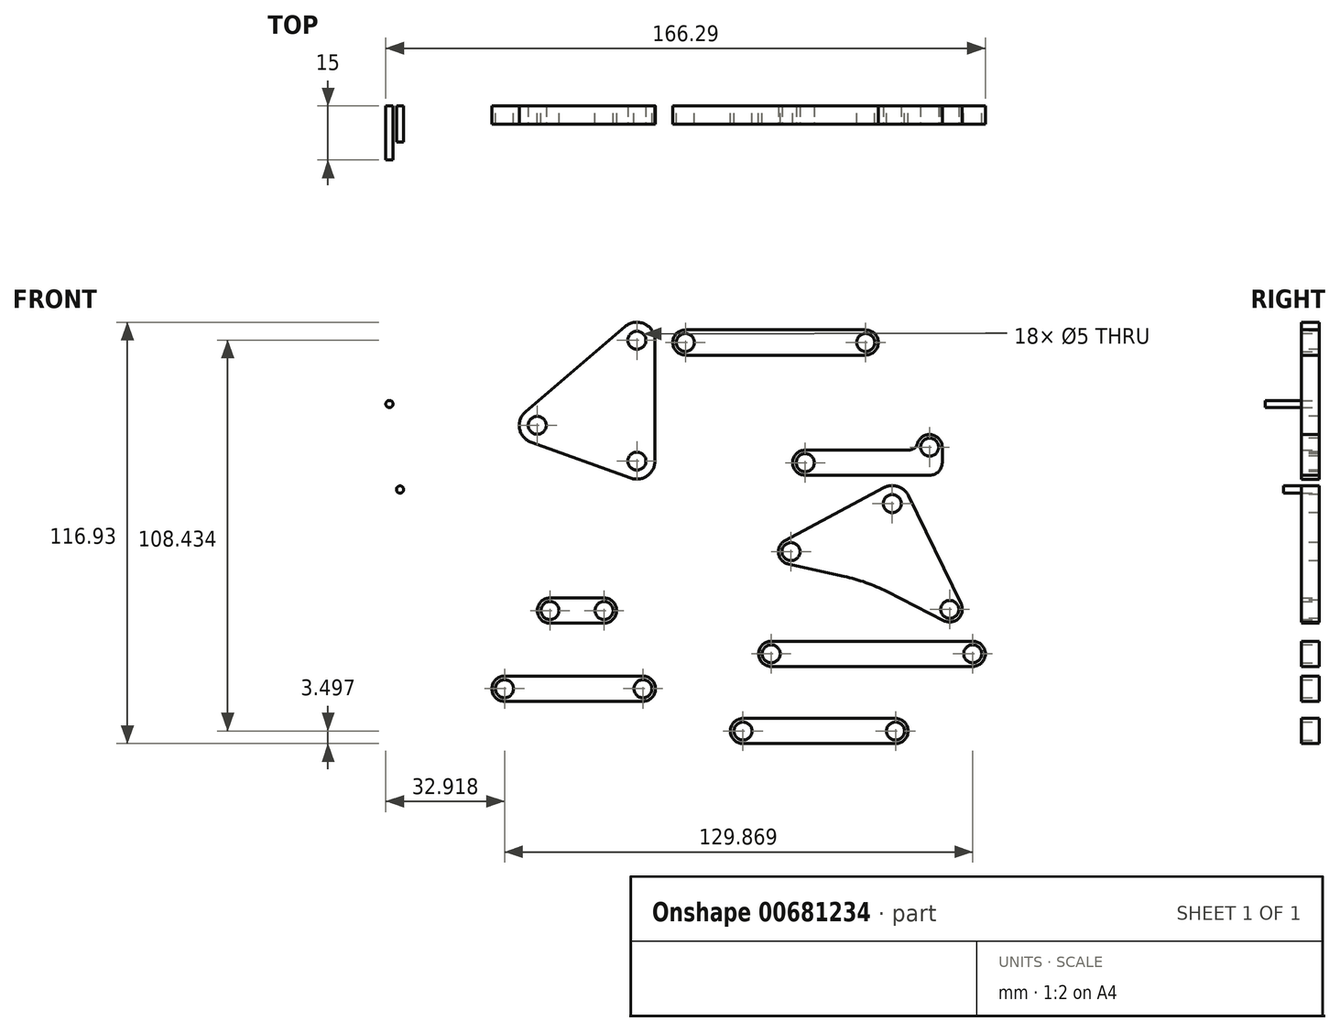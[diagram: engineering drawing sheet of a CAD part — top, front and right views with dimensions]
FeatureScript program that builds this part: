
annotation { "Feature Type Name" : "Feature", "Feature Type Description" : "" }
export const myFeature = defineFeature(function(context is Context, id is Id, definition is map)
    precondition{}
    {
        {
            var Q0;
            Q0=qCreatedBy(makeId("Front.planeOp"),FACE);
            var sketch = newSketch(context, id + "F0", { "sketchPlane" : qUnion([Q0])});
            skLineSegment(sketch, "E0", {"start": v(-19.3, 64.97) * mm, "end": v(-19.3, 13.47) * mm});
            skLineSegment(sketch, "E1", {"start": v(-19.3, 13.47) * mm, "end": v(-61.74, 28.74) * mm});
            skLineSegment(sketch, "E2", {"start": v(-61.74, 28.74) * mm, "end": v(-19.3, 64.97) * mm});
            skSolve(sketch);
        }
        {
            var Q0;
            Q0=makeQuery(id+"F0.imprint","IMPRINT",FACE,{"disambiguationData":[TD([[makeQuery(id+"F0.imprint","IMPRINT",EDGE,{"derivedFrom":sQuery(id+"F0.wireOp",EDGE,"E0")}),-1.0]])]});
            extrude(context, id + "F1", {"entities" : qUnion([Q0]), "depth" : 5 * mm, "offsetDistance" : 25 * mm});
        }
        {
            var Q0;
            Q0=makeQuery(id+"F1.opExtrude","SWEPT_EDGE",EDGE,{"disambiguationData":[OSD([sQuery(id+"F0.wireOp",EDGE,"E0"),sQuery(id+"F0.wireOp",EDGE,"E2")])]});
            var Q1;
            Q1=makeQuery(id+"F1.opExtrude","SWEPT_EDGE",EDGE,{"disambiguationData":[OSD([sQuery(id+"F0.wireOp",EDGE,"E0"),sQuery(id+"F0.wireOp",EDGE,"E1")])]});
            var Q2;
            Q2=makeQuery(id+"F1.opExtrude","SWEPT_EDGE",EDGE,{"disambiguationData":[OSD([sQuery(id+"F0.wireOp",EDGE,"E1"),sQuery(id+"F0.wireOp",EDGE,"E2")])]});
            fillet(context, id + "F2", {"entities" : qUnion([Q0, Q1, Q2]), "radius" : 5 * mm, "tangentPropagation" : true, "allowEdgeOverflow" : false});
        }
        {
            var Q0;
            Q0=makeQuery(id+"F1.opExtrude","CAP_FACE",FACE,{"disambiguationData":[OSD([sQuery(id+"F0.wireOp",EDGE,"E0"),sQuery(id+"F0.wireOp",EDGE,"E1"),sQuery(id+"F0.wireOp",EDGE,"E2")])],"isStart":false});
            var sketch = newSketch(context, id + "F3", { "sketchPlane" : qUnion([Q0])});
            skCircle(sketch, "E3", {"center": v(-24.3, 54.13) * mm, "radius": 2.5 * mm});
            skCircle(sketch, "E4", {"center": v(-24.3, 20.59) * mm, "radius": 2.5 * mm});
            skCircle(sketch, "E5", {"center": v(-51.95, 30.53) * mm, "radius": 2.5 * mm});
            skSolve(sketch);
        }
        {
            var Q0;
            Q0 = qSketchRegion(id + "F3", true);
            extrude(context, id + "F4", {"entities" : qUnion([Q0]), "operationType" : NewBodyOperationType.REMOVE, "oppositeDirection" : true, "depth" : 25 * mm, "offsetDistance" : 25 * mm});
        }
        {
            var Q0;
            Q0=qCreatedBy(makeId("Front.planeOp"),FACE);
            var sketch = newSketch(context, id + "F5", { "sketchPlane" : qUnion([Q0])});
            skLineSegment(sketch, "E6", {"start": v(22.4, 16.66) * mm, "end": v(60.4, 16.66) * mm});
            skLineSegment(sketch, "E7", {"start": v(60.4, 16.66) * mm, "end": v(60.4, 24.46) * mm});
            skLineSegment(sketch, "E8.0", {"start": v(22.4, 23.66) * mm, "end": v(53.4, 23.66) * mm});
            skLineSegment(sketch, "E9.0", {"start": v(53.4, 23.66) * mm, "end": v(53.4, 24.46) * mm});
            skArc(sketch, "E10", {"start": v(60.4, 24.46) * mm, "mid": v(56.9, 27.96) * mm, "end": v(53.4, 24.46) * mm});
            skArc(sketch, "E11", {"start": v(22.4, 23.66) * mm, "mid": v(18.9, 20.16) * mm, "end": v(22.4, 16.66) * mm});
            skSolve(sketch);
        }
        {
            var Q0;
            Q0=makeQuery(id+"F5.imprint","IMPRINT",FACE,{"disambiguationData":[TD([[makeQuery(id+"F5.imprint","IMPRINT",EDGE,{"derivedFrom":sQuery(id+"F5.wireOp",EDGE,"E6")}),1.0]])]});
            extrude(context, id + "F6", {"entities" : qUnion([Q0]), "depth" : 5 * mm, "offsetDistance" : 25 * mm});
        }
        {
            var Q0;
            Q0=makeQuery(id+"F6.opExtrude","SWEPT_EDGE",EDGE,{"disambiguationData":[OSD([sQuery(id+"F5.wireOp",EDGE,"E6"),sQuery(id+"F5.wireOp",EDGE,"E7")])]});
            fillet(context, id + "F7", {"entities" : qUnion([Q0]), "radius" : 3.5 * mm, "tangentPropagation" : true, "allowEdgeOverflow" : false});
        }
        {
            var Q0;
            Q0=makeQuery(id+"F6.opExtrude","SWEPT_EDGE",EDGE,{"disambiguationData":[OSD([sQuery(id+"F5.wireOp",EDGE,"E8.0"),sQuery(id+"F5.wireOp",EDGE,"E9.0")])]});
            fillet(context, id + "F8", {"entities" : qUnion([Q0]), "radius" : 2.5 * mm, "tangentPropagation" : true, "allowEdgeOverflow" : false});
        }
        {
            var Q0;
            Q0=makeQuery(id+"F6.opExtrude","CAP_FACE",FACE,{"disambiguationData":[OSD([sQuery(id+"F5.wireOp",EDGE,"E6"),sQuery(id+"F5.wireOp",EDGE,"E7"),sQuery(id+"F5.wireOp",EDGE,"E8.0"),sQuery(id+"F5.wireOp",EDGE,"E9.0"),sQuery(id+"F5.wireOp",EDGE,"E10"),sQuery(id+"F5.wireOp",EDGE,"E11")])],"isStart":false});
            var sketch = newSketch(context, id + "F9", { "sketchPlane" : qUnion([Q0])});
            skCircle(sketch, "E12", {"center": v(22.4, 20.16) * mm, "radius": 2.5 * mm});
            skCircle(sketch, "E13", {"center": v(56.9, 24.46) * mm, "radius": 2.5 * mm});
            skSolve(sketch);
        }
        {
            var Q0;
            Q0=makeQuery(id+"F9.imprint","IMPRINT",FACE,{"disambiguationData":[TD([[makeQuery(id+"F9.imprint","IMPRINT",EDGE,{"derivedFrom":sQuery(id+"F9.wireOp",EDGE,"E12")}),1.0]])]});
            var Q1;
            Q1=makeQuery(id+"F9.imprint","IMPRINT",FACE,{"disambiguationData":[TD([[makeQuery(id+"F9.imprint","IMPRINT",EDGE,{"derivedFrom":sQuery(id+"F9.wireOp",EDGE,"E13")}),1.0]])]});
            extrude(context, id + "F10", {"entities" : qUnion([Q0, Q1]), "operationType" : NewBodyOperationType.REMOVE, "oppositeDirection" : true, "depth" : 25 * mm, "offsetDistance" : 25 * mm});
        }
        {
            var Q0;
            Q0=qCreatedBy(makeId("Front.planeOp"),FACE);
            var sketch = newSketch(context, id + "F11", { "sketchPlane" : qUnion([Q0])});
            skLineSegment(sketch, "E14.bottom", {"start": v(-48.42, -24.38) * mm, "end": v(-33.42, -24.38) * mm});
            skLineSegment(sketch, "E14.top", {"start": v(-48.42, -17.38) * mm, "end": v(-33.42, -17.38) * mm});
            skArc(sketch, "E15", {"start": v(-48.42, -17.38) * mm, "mid": v(-51.92, -20.88) * mm, "end": v(-48.42, -24.38) * mm});
            skArc(sketch, "E16", {"start": v(-33.42, -24.38) * mm, "mid": v(-29.92, -20.88) * mm, "end": v(-33.42, -17.38) * mm});
            skCircle(sketch, "E17", {"center": v(-48.42, -20.88) * mm, "radius": 2.5 * mm});
            skCircle(sketch, "E18", {"center": v(-33.42, -20.88) * mm, "radius": 2.5 * mm});
            skSolve(sketch);
        }
        {
            var Q0;
            Q0=makeQuery(id+"F11.imprint","IMPRINT",FACE,{"disambiguationData":[TD([[makeQuery(id+"F11.imprint","IMPRINT",EDGE,{"derivedFrom":sQuery(id+"F11.wireOp",EDGE,"E14.bottom")}),1.0]])]});
            extrude(context, id + "F12", {"entities" : qUnion([Q0]), "depth" : 5 * mm, "offsetDistance" : 25 * mm});
        }
        {
            var Q0;
            Q0=qCreatedBy(makeId("Front.planeOp"),FACE);
            var sketch = newSketch(context, id + "F13", { "sketchPlane" : qUnion([Q0])});
            skLineSegment(sketch, "E19.bottom", {"start": v(-10.85, 57) * mm, "end": v(39.15, 57) * mm});
            skLineSegment(sketch, "E19.top", {"start": v(-10.85, 50) * mm, "end": v(39.15, 50) * mm});
            skArc(sketch, "E20", {"start": v(-10.85, 57) * mm, "mid": v(-14.35, 53.5) * mm, "end": v(-10.85, 50) * mm});
            skArc(sketch, "E21", {"start": v(39.15, 50) * mm, "mid": v(42.65, 53.5) * mm, "end": v(39.15, 57) * mm});
            skCircle(sketch, "E22", {"center": v(-10.85, 53.5) * mm, "radius": 2.5 * mm});
            skCircle(sketch, "E23", {"center": v(39.15, 53.5) * mm, "radius": 2.5 * mm});
            skSolve(sketch);
        }
        {
            var Q0;
            Q0=makeQuery(id+"F13.imprint","IMPRINT",FACE,{"disambiguationData":[TD([[makeQuery(id+"F13.imprint","IMPRINT",EDGE,{"derivedFrom":sQuery(id+"F13.wireOp",EDGE,"E19.bottom")}),-1.0]])]});
            extrude(context, id + "F14", {"entities" : qUnion([Q0]), "depth" : 5 * mm, "offsetDistance" : 25 * mm});
        }
        {
            var Q0;
            Q0=qCreatedBy(makeId("Front.planeOp"),FACE);
            var sketch = newSketch(context, id + "F15", { "sketchPlane" : qUnion([Q0])});
            skLineSegment(sketch, "E24.bottom", {"start": v(12.94, -36.38) * mm, "end": v(68.84, -36.38) * mm});
            skLineSegment(sketch, "E24.top", {"start": v(12.94, -29.38) * mm, "end": v(68.84, -29.38) * mm});
            skArc(sketch, "E25", {"start": v(12.94, -29.38) * mm, "mid": v(9.44, -32.88) * mm, "end": v(12.94, -36.38) * mm});
            skArc(sketch, "E26", {"start": v(68.84, -36.38) * mm, "mid": v(72.34, -32.88) * mm, "end": v(68.84, -29.38) * mm});
            skCircle(sketch, "E27", {"center": v(12.94, -32.88) * mm, "radius": 2.5 * mm});
            skCircle(sketch, "E28", {"center": v(68.84, -32.88) * mm, "radius": 2.5 * mm});
            skSolve(sketch);
        }
        {
            var Q0;
            Q0=makeQuery(id+"F15.imprint","IMPRINT",FACE,{"disambiguationData":[TD([[makeQuery(id+"F15.imprint","IMPRINT",EDGE,{"derivedFrom":sQuery(id+"F15.wireOp",EDGE,"E24.bottom")}),1.0]])]});
            extrude(context, id + "F16", {"entities" : qUnion([Q0]), "depth" : 5 * mm, "offsetDistance" : 25 * mm});
        }
        {
            var Q0;
            Q0=qCreatedBy(makeId("Front.planeOp"),FACE);
            var sketch = newSketch(context, id + "F17", { "sketchPlane" : qUnion([Q0])});
            skLineSegment(sketch, "E29.bottom", {"start": v(-61.03, -46.07) * mm, "end": v(-22.63, -46.07) * mm});
            skLineSegment(sketch, "E29.top", {"start": v(-61.03, -39.07) * mm, "end": v(-22.63, -39.07) * mm});
            skArc(sketch, "E30", {"start": v(-61.03, -39.07) * mm, "mid": v(-64.53, -42.57) * mm, "end": v(-61.03, -46.07) * mm});
            skArc(sketch, "E31", {"start": v(-22.63, -46.07) * mm, "mid": v(-19.13, -42.57) * mm, "end": v(-22.63, -39.07) * mm});
            skCircle(sketch, "E32", {"center": v(-61.03, -42.57) * mm, "radius": 2.5 * mm});
            skCircle(sketch, "E33", {"center": v(-22.63, -42.57) * mm, "radius": 2.5 * mm});
            skSolve(sketch);
        }
        {
            var Q0;
            Q0=makeQuery(id+"F17.imprint","IMPRINT",FACE,{"disambiguationData":[TD([[makeQuery(id+"F17.imprint","IMPRINT",EDGE,{"derivedFrom":sQuery(id+"F17.wireOp",EDGE,"E29.bottom")}),1.0]])]});
            extrude(context, id + "F18", {"entities" : qUnion([Q0]), "depth" : 5 * mm, "offsetDistance" : 25 * mm});
        }
        {
            var Q0;
            Q0=qCreatedBy(makeId("Front.planeOp"),FACE);
            var sketch = newSketch(context, id + "F19", { "sketchPlane" : qUnion([Q0])});
            skLineSegment(sketch, "E34.bottom", {"start": v(5.13, -57.8) * mm, "end": v(47.43, -57.8) * mm});
            skLineSegment(sketch, "E34.top", {"start": v(5.13, -50.8) * mm, "end": v(47.43, -50.8) * mm});
            skArc(sketch, "E35", {"start": v(5.13, -50.8) * mm, "mid": v(1.63, -54.3) * mm, "end": v(5.13, -57.8) * mm});
            skArc(sketch, "E36", {"start": v(47.43, -57.8) * mm, "mid": v(50.93, -54.3) * mm, "end": v(47.43, -50.8) * mm});
            skCircle(sketch, "E37", {"center": v(5.13, -54.3) * mm, "radius": 2.5 * mm});
            skCircle(sketch, "E38", {"center": v(47.43, -54.3) * mm, "radius": 2.5 * mm});
            skSolve(sketch);
        }
        {
            var Q0;
            Q0=makeQuery(id+"F19.imprint","IMPRINT",FACE,{"disambiguationData":[TD([[makeQuery(id+"F19.imprint","IMPRINT",EDGE,{"derivedFrom":sQuery(id+"F19.wireOp",EDGE,"E34.bottom")}),1.0]])]});
            extrude(context, id + "F20", {"entities" : qUnion([Q0]), "depth" : 5 * mm, "offsetDistance" : 25 * mm});
        }
        {
            var Q0;
            Q0=qCreatedBy(makeId("Front.planeOp"),FACE);
            var sketch = newSketch(context, id + "F21", { "sketchPlane" : qUnion([Q0])});
            skLineSegment(sketch, "E39", {"start": v(8.45, -5.9) * mm, "end": v(48.75, 15.66) * mm});
            skLineSegment(sketch, "E40", {"start": v(48.75, 15.66) * mm, "end": v(70.17, -28.41) * mm});
            skLineSegment(sketch, "E41", {"start": v(8.45, -5.9) * mm, "end": v(39.37, -12.74) * mm});
            skLineSegment(sketch, "E42", {"start": v(39.37, -12.74) * mm, "end": v(70.17, -28.41) * mm});
            skSolve(sketch);
        }
        {
            var Q0;
            Q0=makeQuery(id+"F21.imprint","IMPRINT",FACE,{"disambiguationData":[TD([[makeQuery(id+"F21.imprint","IMPRINT",EDGE,{"derivedFrom":sQuery(id+"F21.wireOp",EDGE,"E39")}),-1.0]])]});
            extrude(context, id + "F22", {"entities" : qUnion([Q0]), "depth" : 5 * mm, "offsetDistance" : 25 * mm});
        }
        {
            var Q0;
            Q0=makeQuery(id+"F22.opExtrude","SWEPT_EDGE",EDGE,{"disambiguationData":[OSD([sQuery(id+"F21.wireOp",EDGE,"E41"),sQuery(id+"F21.wireOp",EDGE,"E42")])]});
            fillet(context, id + "F23", {"entities" : qUnion([Q0]), "radius" : 50 * mm, "tangentPropagation" : true, "allowEdgeOverflow" : false});
        }
        {
            var Q0;
            Q0=makeQuery(id+"F22.opExtrude","SWEPT_EDGE",EDGE,{"disambiguationData":[OSD([sQuery(id+"F21.wireOp",EDGE,"E39"),sQuery(id+"F21.wireOp",EDGE,"E40")])]});
            fillet(context, id + "F24", {"entities" : qUnion([Q0]), "radius" : 5 * mm, "tangentPropagation" : true, "allowEdgeOverflow" : false});
        }
        {
            var Q0;
            Q0=makeQuery(id+"F22.opExtrude","SWEPT_EDGE",EDGE,{"disambiguationData":[OSD([sQuery(id+"F21.wireOp",EDGE,"E39"),sQuery(id+"F21.wireOp",EDGE,"E41")])]});
            var Q1;
            Q1=makeQuery(id+"F22.opExtrude","SWEPT_EDGE",EDGE,{"disambiguationData":[OSD([sQuery(id+"F21.wireOp",EDGE,"E40"),sQuery(id+"F21.wireOp",EDGE,"E42")])]});
            fillet(context, id + "F25", {"entities" : qUnion([Q0, Q1]), "radius" : 3.5 * mm, "tangentPropagation" : true, "allowEdgeOverflow" : false});
        }
        {
            var Q0;
            Q0=makeQuery(id+"F22.opExtrude","CAP_FACE",FACE,{"disambiguationData":[OSD([sQuery(id+"F21.wireOp",EDGE,"E39"),sQuery(id+"F21.wireOp",EDGE,"E40"),sQuery(id+"F21.wireOp",EDGE,"E41"),sQuery(id+"F21.wireOp",EDGE,"E42")])],"isStart":false});
            var sketch = newSketch(context, id + "F26", { "sketchPlane" : qUnion([Q0])});
            skCircle(sketch, "E43", {"center": v(18.44, -4.52) * mm, "radius": 2.5 * mm});
            skCircle(sketch, "E44", {"center": v(46.52, 8.8) * mm, "radius": 2.5 * mm});
            skCircle(sketch, "E45", {"center": v(62.46, -20.56) * mm, "radius": 2.5 * mm});
            skSolve(sketch);
        }
        {
            var Q0;
            Q0=makeQuery(id+"F26.imprint","IMPRINT",FACE,{"disambiguationData":[TD([[makeQuery(id+"F26.imprint","IMPRINT",EDGE,{"derivedFrom":sQuery(id+"F26.wireOp",EDGE,"E44")}),1.0]])]});
            var Q1;
            Q1=makeQuery(id+"F26.imprint","IMPRINT",FACE,{"disambiguationData":[TD([[makeQuery(id+"F26.imprint","IMPRINT",EDGE,{"derivedFrom":sQuery(id+"F26.wireOp",EDGE,"E43")}),1.0]])]});
            var Q2;
            Q2=makeQuery(id+"F26.imprint","IMPRINT",FACE,{"disambiguationData":[TD([[makeQuery(id+"F26.imprint","IMPRINT",EDGE,{"derivedFrom":sQuery(id+"F26.wireOp",EDGE,"E45")}),1.0]])]});
            extrude(context, id + "F27", {"entities" : qUnion([Q0, Q1, Q2]), "operationType" : NewBodyOperationType.REMOVE, "oppositeDirection" : true, "depth" : 25 * mm, "offsetDistance" : 25 * mm});
        }
        {
            var Q0;
            Q0=qCreatedBy(makeId("Front.planeOp"),FACE);
            var sketch = newSketch(context, id + "F28", { "sketchPlane" : qUnion([Q0])});
            skCircle(sketch, "E46", {"center": v(-92.95, 36.43) * mm, "radius": 1 * mm});
            skSolve(sketch);
        }
        {
            var Q0;
            Q0=makeQuery(id+"F28.imprint","IMPRINT",FACE,{"disambiguationData":[TD([[makeQuery(id+"F28.imprint","IMPRINT",EDGE,{"derivedFrom":sQuery(id+"F28.wireOp",EDGE,"E46")}),1.0]])]});
            extrude(context, id + "F29", {"entities" : qUnion([Q0]), "depth" : 15 * mm, "offsetDistance" : 25 * mm});
        }
        {
            var Q0;
            Q0=qCreatedBy(makeId("Front.planeOp"),FACE);
            var sketch = newSketch(context, id + "F30", { "sketchPlane" : qUnion([Q0])});
            skCircle(sketch, "E47", {"center": v(-90, 12.7) * mm, "radius": 1 * mm});
            skSolve(sketch);
        }
        {
            var Q0;
            Q0=makeQuery(id+"F30.imprint","IMPRINT",FACE,{"disambiguationData":[TD([[makeQuery(id+"F30.imprint","IMPRINT",EDGE,{"derivedFrom":sQuery(id+"F30.wireOp",EDGE,"E47")}),1.0]])]});
            extrude(context, id + "F31", {"entities" : qUnion([Q0]), "depth" : 10 * mm, "offsetDistance" : 25 * mm});
        }
    });
